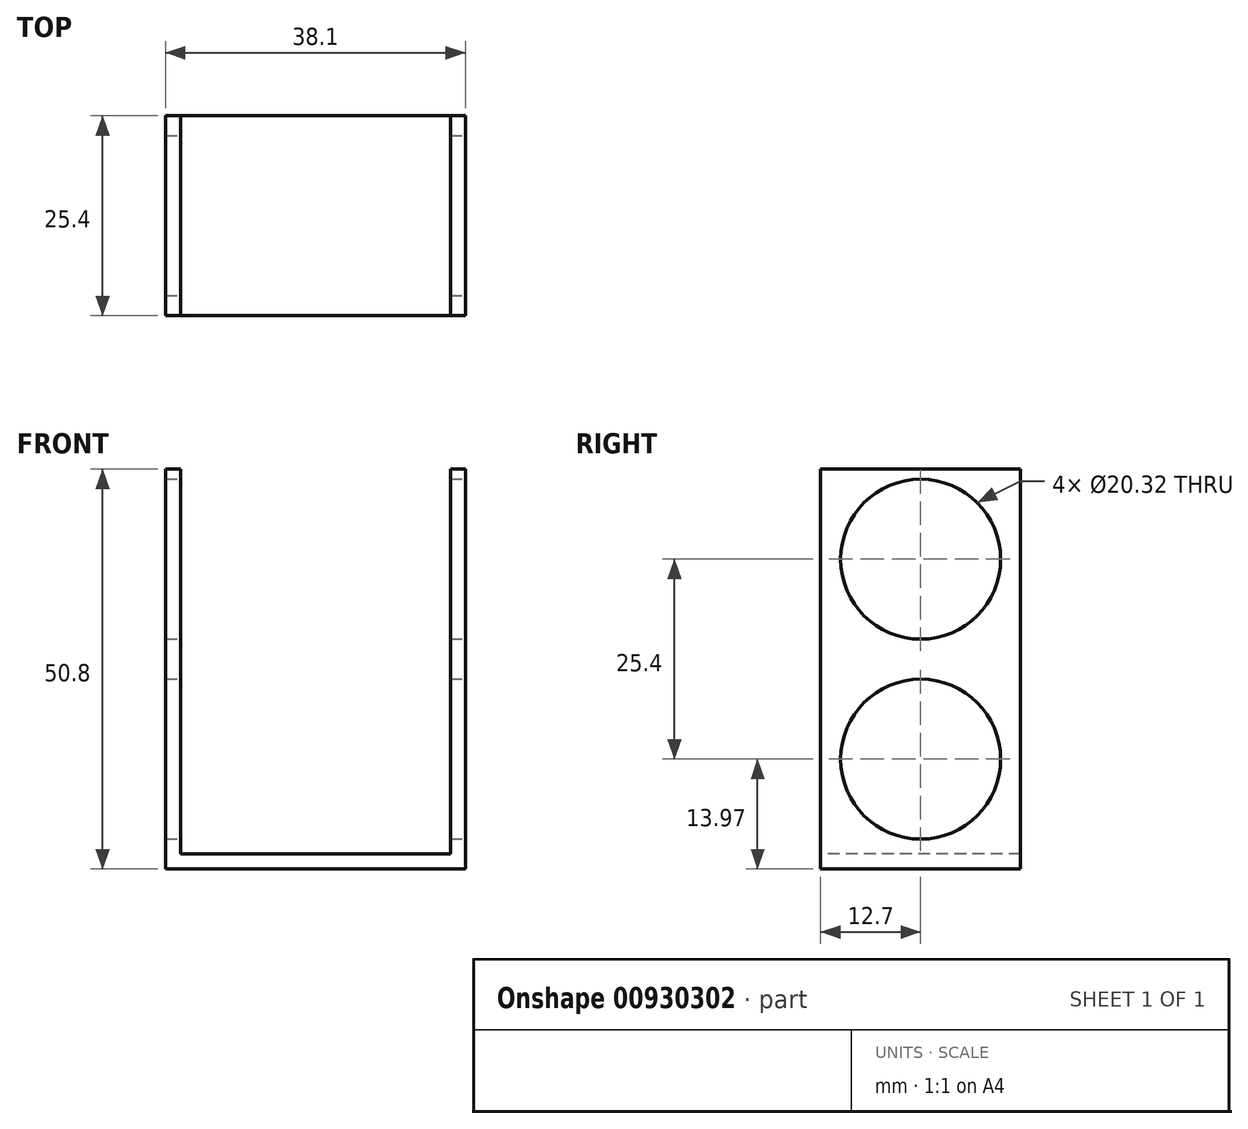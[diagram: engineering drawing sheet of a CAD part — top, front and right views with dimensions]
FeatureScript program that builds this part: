
annotation { "Feature Type Name" : "Feature", "Feature Type Description" : "" }
export const myFeature = defineFeature(function(context is Context, id is Id, definition is map)
    precondition{}
    {
        {
            var Q0;
            Q0=qCreatedBy(makeId("Top.planeOp"),FACE);
            var sketch = newSketch(context, id + "F0", { "sketchPlane" : qUnion([Q0])});
            skLineSegment(sketch, "E0.bottom", {"start": v(0, 0) * mm, "end": v(38.1, 0) * mm});
            skLineSegment(sketch, "E0.top", {"start": v(0, 25.4) * mm, "end": v(38.1, 25.4) * mm});
            skLineSegment(sketch, "E0.left", {"start": v(0, 0) * mm, "end": v(0, 25.4) * mm});
            skLineSegment(sketch, "E0.right", {"start": v(38.1, 0) * mm, "end": v(38.1, 25.4) * mm});
            skSolve(sketch);
        }
        {
            var Q0;
            Q0 = qSketchRegion(id + "F0", true);
            extrude(context, id + "F1", {"entities" : qUnion([Q0]), "depth" : 50.8 * mm, "offsetDistance" : 25.4 * mm});
        }
        {
            var Q0;
            Q0=makeQuery(id+"F1.opExtrude","SWEPT_FACE",FACE,{"disambiguationData":[OSD([sQuery(id+"F0.wireOp",EDGE,"E0.bottom")])]});
            var sketch = newSketch(context, id + "F2", { "sketchPlane" : qUnion([Q0])});
            skLineSegment(sketch, "E1.bottom", {"start": v(1.9, 50.8) * mm, "end": v(36.2, 50.8) * mm});
            skLineSegment(sketch, "E1.top", {"start": v(1.9, 1.9) * mm, "end": v(36.2, 1.9) * mm});
            skLineSegment(sketch, "E1.left", {"start": v(1.9, 50.8) * mm, "end": v(1.9, 1.9) * mm});
            skLineSegment(sketch, "E1.right", {"start": v(36.2, 50.8) * mm, "end": v(36.2, 1.9) * mm});
            skSolve(sketch);
        }
        {
            var Q0;
            Q0=makeQuery(id+"F2.imprint","IMPRINT",FACE,{"disambiguationData":[TD([[makeQuery(id+"F2.imprint","IMPRINT",EDGE,{"derivedFrom":sQuery(id+"F2.wireOp",EDGE,"E1.bottom")}),-1.0]])]});
            extrude(context, id + "F3", {"entities" : qUnion([Q0]), "operationType" : NewBodyOperationType.REMOVE, "oppositeDirection" : true, "depth" : 25.4 * mm, "offsetDistance" : 25.4 * mm});
        }
        {
            var Q0;
            Q0=makeQuery(id+"F1.opExtrude","SWEPT_FACE",FACE,{"disambiguationData":[OSD([sQuery(id+"F0.wireOp",EDGE,"E0.right")])]});
            var sketch = newSketch(context, id + "F4", { "sketchPlane" : qUnion([Q0])});
            skCircle(sketch, "E2", {"center": v(12.7, 39.37) * mm, "radius": 10.16 * mm});
            skCircle(sketch, "E3", {"center": v(12.7, 13.97) * mm, "radius": 10.16 * mm});
            skSolve(sketch);
        }
        {
            var Q0;
            Q0=makeQuery(id+"F4.imprint","IMPRINT",FACE,{"disambiguationData":[TD([[makeQuery(id+"F4.imprint","IMPRINT",EDGE,{"derivedFrom":sQuery(id+"F4.wireOp",EDGE,"E2")}),1.0]])]});
            var Q1;
            Q1=makeQuery(id+"F4.imprint","IMPRINT",FACE,{"disambiguationData":[TD([[makeQuery(id+"F4.imprint","IMPRINT",EDGE,{"derivedFrom":sQuery(id+"F4.wireOp",EDGE,"E3")}),1.0]])]});
            extrude(context, id + "F5", {"entities" : qUnion([Q0, Q1]), "operationType" : NewBodyOperationType.REMOVE, "oppositeDirection" : true, "depth" : 50.8 * mm, "offsetDistance" : 25.4 * mm});
        }
    });
